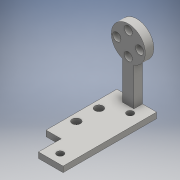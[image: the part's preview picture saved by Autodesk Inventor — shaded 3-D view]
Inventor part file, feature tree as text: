
AUTODESK INVENTOR PART (.ipt)
format: ipt  version: 2016 (Build 200138000, 138)  size: 232,960 bytes
history: native  units: mm
features: sketch x8, extrude x6, hole x2
ambient origin geometry x8: Origin, YZ Plane, XZ Plane, XY Plane, X Axis, Y Axis, Z Axis, Center Point
bodies: Solid1 (feature_tree)
feature tree (16):
  extrude  "Extrusion1"  Depth=4.35mm
  extrude  "Extrusion2"  Depth=6.0mm
  extrude  "Extrusion3"  Depth=6.0mm
  hole  "Hole1"  [1 undecoded]
  hole  "Hole2"  [1 undecoded]
  extrude  "Extrusion4"  Depth=6.0mm
  extrude  "Extrusion5"  Depth=48.0mm TaperAngle=0.0deg
  extrude  "Extrusion6"  Depth=1.5mm
  sketch  "Sketch1"  dims[d0=18.0mm d1=4.35mm]
  sketch  "Sketch2"  dims[d2=6.0mm d3=4.35mm]
  sketch  "Sketch3"  dims[d4=6.0mm d5=4.35mm]
  sketch  "Sketch4"  dims[d6=6.0mm d7=4.35mm]
  sketch  "Sketch5"  dims[d8=6.0mm d9=3.0mm d10=0.0mm]
  sketch  "Sketch6"  dims[d13=6.0mm d14=6.0mm]
  sketch  "Sketch7"  dims[d15=1.5mm d16=48.0mm d17=0.0mm]
  sketch  "Sketch8"  dims[d18=3.5mm d19=3.5mm d21=1.5mm d22=0.0mm d23=3.5mm d26=3.5mm d28=3.0mm d29=3.5mm d30=6.0mm d31=4.0mm d32=2.0mm d33=90.0deg d34=8.0mm d35=20.594885mm d36=3.0mm d43=4.0mm d44=4.0mm d45=6.5mm d46=6.5mm d47=12.0mm d48=4.35mm d49=6.0mm d50=4.0mm d51=4.35mm d52=6.0mm d53=4.0mm d54=4.35mm d55=6.0mm d56=4.0mm d57=2.0mm d58=90.0deg d59=8.0mm d60=20.594885mm d61=13.0mm d64=3.0mm d65=0.0mm d66=20.0mm d67=4.35mm d68=6.0mm d69=4.35mm d70=6.0mm d71=4.35mm d72=6.0mm d73=1.5mm d74=0.0mm d75=3.5mm d76=1.5mm d77=0.0mm d78=37.0mm]
note: 2 required parameter values undecoded (feature->parameter linkage not recoverable at this tier; creation-order binding heuristic only, values carry confidence <= 0.55)
